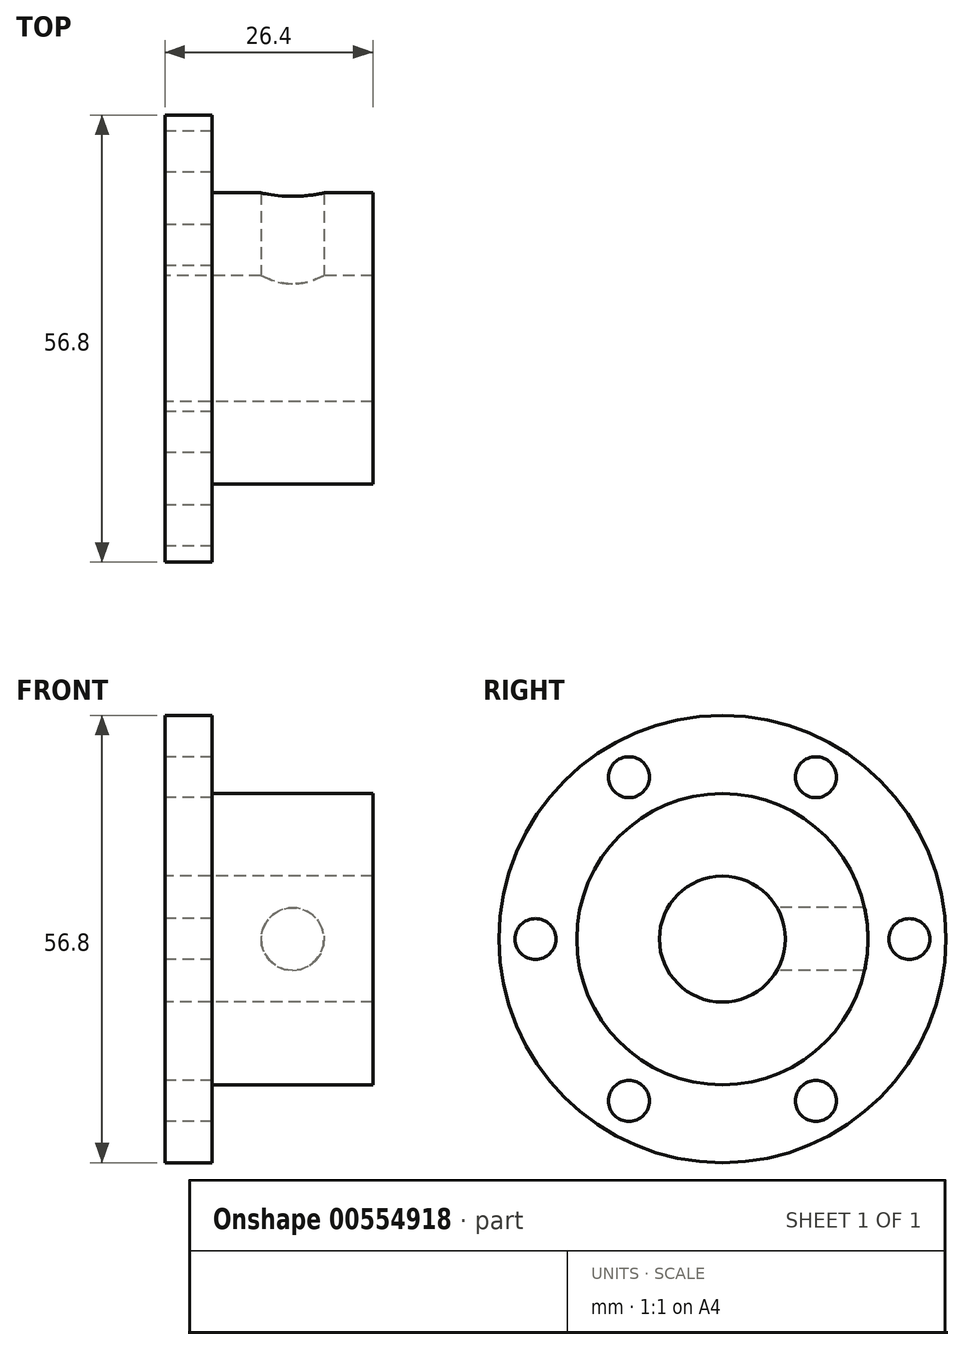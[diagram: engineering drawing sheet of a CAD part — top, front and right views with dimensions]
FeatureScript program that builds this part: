
annotation { "Feature Type Name" : "Feature", "Feature Type Description" : "" }
export const myFeature = defineFeature(function(context is Context, id is Id, definition is map)
    precondition{}
    {
        {
            var Q0;
            Q0=qCreatedBy(makeId("Front.planeOp"),FACE);
            var sketch = newSketch(context, id + "F0", { "sketchPlane" : qUnion([Q0])});
            skLineSegment(sketch, "E0", {"start": v(-18.27, 0) * mm, "end": v(528.92, 0) * mm});
            skLineSegment(sketch, "E1", {"start": v(-18.27, 8) * mm, "end": v(8.13, 8) * mm});
            skLineSegment(sketch, "E2", {"start": v(8.13, 8) * mm, "end": v(8.13, 18.5) * mm});
            skLineSegment(sketch, "E3", {"start": v(8.13, 18.5) * mm, "end": v(-12.27, 18.5) * mm});
            skLineSegment(sketch, "E4", {"start": v(-12.27, 18.5) * mm, "end": v(-12.27, 28.4) * mm});
            skLineSegment(sketch, "E5", {"start": v(-12.27, 28.4) * mm, "end": v(-18.27, 28.4) * mm});
            skLineSegment(sketch, "E6", {"start": v(-18.27, 28.4) * mm, "end": v(-18.27, 8) * mm});
            skSolve(sketch);
        }
        {
            var Q0;
            Q0=qSketchRegion(id+"F0",true);
            var Q1;
            Q1=sQuery(id+"F0.wireOp",EDGE,"E0");
            revolve(context, id + "F1", {"entities" : qUnion([Q0]), "axis" : qUnion([Q1]), "revolveType" : RevolveType.FULL});
        }
        {
            var Q0;
            Q0=makeQuery(id+"F1.opRevolve","SWEPT_FACE",FACE,{"disambiguationData":[OSD([sQuery(id+"F0.wireOp",EDGE,"E6")])]});
            var sketch = newSketch(context, id + "F2", { "sketchPlane" : qUnion([Q0])});
            skLineSegment(sketch, "E7", {"start": v(0, 0) * mm, "end": v(-22.14, 0) * mm, "construction": true});
            skCircle(sketch, "E8", {"center": v(-23.75, 0) * mm, "radius": 2.6 * mm});
            skCircle(sketch, "E9.1.0", {"center": v(-11.88, -20.57) * mm, "radius": 2.6 * mm});
            skCircle(sketch, "E9.2.0", {"center": v(11.87, -20.57) * mm, "radius": 2.6 * mm});
            skCircle(sketch, "E9.3.0", {"center": v(23.75, 0) * mm, "radius": 2.6 * mm});
            skCircle(sketch, "E9.4.0", {"center": v(11.88, 20.57) * mm, "radius": 2.6 * mm});
            skCircle(sketch, "E9.5.0", {"center": v(-11.88, 20.57) * mm, "radius": 2.6 * mm});
            skPoint(sketch, "E9.center", {"position": v(0, 0) * mm});
            skSolve(sketch);
        }
        {
            var Q0;
            Q0=qSketchRegion(id+"F2",true);
            extrude(context, id + "F3", {"entities" : qUnion([Q0]), "operationType" : NewBodyOperationType.REMOVE, "endBound" : BoundingType.THROUGH_ALL, "oppositeDirection" : true, "depth" : 25 * mm, "offsetDistance" : 25 * mm});
        }
        {
            var Q0;
            Q0=qCreatedBy(makeId("Front.planeOp"),FACE);
            var sketch = newSketch(context, id + "F4", { "sketchPlane" : qUnion([Q0])});
            skCircle(sketch, "E10", {"center": v(-2.07, 0) * mm, "radius": 4 * mm});
            skSolve(sketch);
        }
        {
            var Q0;
            Q0=makeQuery(id+"F4.imprint","IMPRINT",FACE,{"disambiguationData":[TD([[makeQuery(id+"F4.imprint","IMPRINT",EDGE,{"derivedFrom":sQuery(id+"F4.wireOp",EDGE,"E10")}),1.0]])]});
            var Q1;
            Q1=sQuery(id+"F4.wireOp",EDGE,"E10");
            extrude(context, id + "F5", {"entities" : qUnion([Q0]), "operationType" : NewBodyOperationType.REMOVE, "surfaceEntities" : qUnion([Q1]), "endBound" : BoundingType.THROUGH_ALL, "oppositeDirection" : true, "depth" : 25 * mm, "offsetDistance" : 25 * mm});
        }
    });
